# Revit family: Hager-UNIVERS-Surface_mounted-IP44-With_Cover-With_DIN-NoHosted-IE-en
name_source: partatom
category: Electrical Equipment
units: mm (PartAtom-declared; Revit-internal decimal feet)

## family parameters
Always vertical = Yes
Cut with Voids When Loaded = No
Maintain Annotation Orientation = No
Panel Configuration = Two Columns, Circuits Across
Part Type = Panelboard
Room Calculation Point = No
Round Connector Dimension = Use Diameter
Shared = No
Work Plane-Based = Yes

## types (20) — shared parameters
Code hager = ADD-EC000214_EU
Default Elevation = 1200 mm
EF000003 - Mounting method = Surface mounted
EF000007 - Colour = White
EF000024 - UV resistant = No
EF000049 - Depth = 165 mm
EF000116 - RAL-number = 9010
EF000118 - With mounting plate = No
EF000218 - Built-in depth = 161 mm  [stored 0.528215 ft]
EF001062 - EMC-version = No
EF001088 - Extension possible = Yes
EF001134 - DIN-rail = Yes
EF004462 - Type of closure = Other
EF005474 - Degree of protection (IP) = IP44
EF006244 - Transparent cover/door = No
EF006306 - With lock = No
EF009212 - Cover model = With notch
EF015776 - Earthing terminal block = No
EF015777 - Neutral terminal block = Yes
EF015941 - Signal passing door = No
ETIM class code = EC000214
ETIM class name = Small distribution board
HG000002-With door or cover = Yes
HG000003-Range = UNIVERS
HG000005-Thickness = 2 mm  [stored 0.00656168 ft]
HG000006-Flush mounted = No
HG000011-Empty rows from bottom = No
HG000012-Door swing angle = 90.00°
HG000013-Door on the left = No
HG000014-Door on the right = Yes
HG000015-Clearance visibility = Yes
HG000016-Door 3D visibility = Yes
HG000017-Distance between poles = 18 mm  [stored 0.0590551 ft]
HG000060-RAL-number = 9010
HG000099-Onfly Template ID = 507532
Manufacturer = Hager
Name BIM&CO = Electricity
Name hager = ADD_Enclosures_EC000214
Reference = Template-Enclosure_EU-EC000214
Uniformat = Low Tension Service & Dist.
Uniformat code = D501001
zero-valued in all types: EF001131 - Inner depth, HG000007-Number of empty columns, HG000008-Number of empty rows

## per-type parameters (varying)
| type | BC_METADATA | EF000008 - Width | EF000040 - Height | EF000266 - Number of rows | EF000332 - Built-in height | EF000846 - Built-in width | EF002950 - Width in number of modular spacings | HG000001-Number of columns | HG000004-Manufacturer reference | HG000009-Double swing door | HG000010-Asymmetric doors | HGEF000266-Number of rows | HGEF002950-Width in number of modular spacings |
| UNIVERS-Surface_mounted_W300_H500_D165_12_Modular_Spacing-FWB31 | {"ObjectGuid":"87d1702a-8fc3-4392-9d8b-29cae2940906","ModelGuid":"894203d7-2d7f-404a-984e-4a048ff082d1","VariantGuid":"fb002c13-881c-4551-97f2-6654b2d32c52","Revision":"#3","VariantName":"UNIVERS-Surface_mounted_W300_H500_D165_12_Modular_Spacing-FWB31"} | 300 mm | 500 mm  [stored 1.64042 ft] | 3 | 500 mm  [stored 1.64042 ft] | 300 mm | 12 | 1 | FWB31 | No | No | 3 | 12 |
| UNIVERS-Surface_mounted_W550_H500_D165_24_Modular_Spacing-FWB32 | {"ObjectGuid":"87d1702a-8fc3-4392-9d8b-29cae2940906","ModelGuid":"894203d7-2d7f-404a-984e-4a048ff082d1","VariantGuid":"cee11cdb-fcee-4029-a44f-e8bf54190ad9","Revision":"#3","VariantName":"UNIVERS-Surface_mounted_W550_H500_D165_24_Modular_Spacing-FWB32"} | 550 mm | 500 mm  [stored 1.64042 ft] | 3 | 500 mm  [stored 1.64042 ft] | 550 mm | 24 | 2 | FWB32 | No | No | 3 | 24 |
| UNIVERS-Surface_mounted_W800_H500_D165_36_Modular_Spacing-FWB33 | {"ObjectGuid":"87d1702a-8fc3-4392-9d8b-29cae2940906","ModelGuid":"894203d7-2d7f-404a-984e-4a048ff082d1","VariantGuid":"9ffd5afd-2b9f-452c-9877-37d7ab24ad53","Revision":"#3","VariantName":"UNIVERS-Surface_mounted_W800_H500_D165_36_Modular_Spacing-FWB33"} | 800 mm  [stored 2.62467 ft] | 500 mm  [stored 1.64042 ft] | 3 | 500 mm  [stored 1.64042 ft] | 800 mm  [stored 2.62467 ft] | 36 | 3 | FWB33 | Yes | Yes | 3 | 36 |
| UNIVERS-Surface_mounted_W1050_H500_D165_48_Modular_Spacing-FWB34 | {"ObjectGuid":"87d1702a-8fc3-4392-9d8b-29cae2940906","ModelGuid":"894203d7-2d7f-404a-984e-4a048ff082d1","VariantGuid":"757fb0db-eacd-4dbe-9c26-48be6830e068","Revision":"#3","VariantName":"UNIVERS-Surface_mounted_W1050_H500_D165_48_Modular_Spacing-FWB34"} | 1050 mm  [stored 3.44488 ft] | 500 mm  [stored 1.64042 ft] | 3 | 500 mm  [stored 1.64042 ft] | 1050 mm  [stored 3.44488 ft] | 48 | 4 | FWB34 | Yes | No | 3 | 48 |
| UNIVERS-Surface_mounted_W300_H650_D165_12_Modular_Spacing-FWB41 | {"ObjectGuid":"87d1702a-8fc3-4392-9d8b-29cae2940906","ModelGuid":"894203d7-2d7f-404a-984e-4a048ff082d1","VariantGuid":"200c4517-b822-4654-bec3-323ac2ee224b","Revision":"#3","VariantName":"UNIVERS-Surface_mounted_W300_H650_D165_12_Modular_Spacing-FWB41"} | 300 mm | 650 mm  [stored 2.13255 ft] | 4 | 650 mm  [stored 2.13255 ft] | 300 mm | 12 | 1 | FWB41 | No | No | 4 | 12 |
| UNIVERS-Surface_mounted_W550_H650_D165_24_Modular_Spacing-FWB42 | {"ObjectGuid":"87d1702a-8fc3-4392-9d8b-29cae2940906","ModelGuid":"894203d7-2d7f-404a-984e-4a048ff082d1","VariantGuid":"df44d009-7728-4836-95ee-009f0ac16905","Revision":"#3","VariantName":"UNIVERS-Surface_mounted_W550_H650_D165_24_Modular_Spacing-FWB42"} | 550 mm | 650 mm  [stored 2.13255 ft] | 4 | 650 mm  [stored 2.13255 ft] | 550 mm | 24 | 2 | FWB42 | No | No | 4 | 24 |
| UNIVERS-Surface_mounted_W800_H650_D165_36_Modular_Spacing-FWB43 | {"ObjectGuid":"87d1702a-8fc3-4392-9d8b-29cae2940906","ModelGuid":"894203d7-2d7f-404a-984e-4a048ff082d1","VariantGuid":"1a2c2fab-c1f9-4678-af95-63d509a17314","Revision":"#3","VariantName":"UNIVERS-Surface_mounted_W800_H650_D165_36_Modular_Spacing-FWB43"} | 800 mm  [stored 2.62467 ft] | 650 mm  [stored 2.13255 ft] | 4 | 650 mm  [stored 2.13255 ft] | 800 mm  [stored 2.62467 ft] | 36 | 3 | FWB43 | Yes | Yes | 4 | 36 |
| UNIVERS-Surface_mounted_W1050_H650_D165_48_Modular_Spacing-FWB44 | {"ObjectGuid":"87d1702a-8fc3-4392-9d8b-29cae2940906","ModelGuid":"894203d7-2d7f-404a-984e-4a048ff082d1","VariantGuid":"95f7c8aa-e01f-4d5c-9763-2ded6d1ccbba","Revision":"#3","VariantName":"UNIVERS-Surface_mounted_W1050_H650_D165_48_Modular_Spacing-FWB44"} | 1050 mm  [stored 3.44488 ft] | 650 mm  [stored 2.13255 ft] | 4 | 650 mm  [stored 2.13255 ft] | 1050 mm  [stored 3.44488 ft] | 48 | 4 | FWB44 | Yes | No | 4 | 48 |
| UNIVERS-Surface_mounted_W300_H800_D165_12_Modular_Spacing-FWB51 | {"ObjectGuid":"87d1702a-8fc3-4392-9d8b-29cae2940906","ModelGuid":"894203d7-2d7f-404a-984e-4a048ff082d1","VariantGuid":"bc364827-2a88-4f4d-b013-22060a447f94","Revision":"#3","VariantName":"UNIVERS-Surface_mounted_W300_H800_D165_12_Modular_Spacing-FWB51"} | 300 mm | 800 mm  [stored 2.62467 ft] | 5 | 800 mm  [stored 2.62467 ft] | 300 mm | 12 | 1 | FWB51 | No | No | 5 | 12 |
| UNIVERS-Surface_mounted_W550_H800_D165_24_Modular_Spacing-FWB52 | {"ObjectGuid":"87d1702a-8fc3-4392-9d8b-29cae2940906","ModelGuid":"894203d7-2d7f-404a-984e-4a048ff082d1","VariantGuid":"4fe331b8-bf32-456e-aabb-ef4181844985","Revision":"#3","VariantName":"UNIVERS-Surface_mounted_W550_H800_D165_24_Modular_Spacing-FWB52"} | 550 mm | 800 mm  [stored 2.62467 ft] | 5 | 800 mm  [stored 2.62467 ft] | 550 mm | 24 | 2 | FWB52 | No | No | 5 | 24 |
| UNIVERS-Surface_mounted_W800_H800_D165_36_Modular_Spacing-FWB53 | {"ObjectGuid":"87d1702a-8fc3-4392-9d8b-29cae2940906","ModelGuid":"894203d7-2d7f-404a-984e-4a048ff082d1","VariantGuid":"a2cdd5c0-b026-411c-bbdb-f125d01b5ec7","Revision":"#3","VariantName":"UNIVERS-Surface_mounted_W800_H800_D165_36_Modular_Spacing-FWB53"} | 800 mm  [stored 2.62467 ft] | 800 mm  [stored 2.62467 ft] | 5 | 800 mm  [stored 2.62467 ft] | 800 mm  [stored 2.62467 ft] | 36 | 3 | FWB53 | Yes | Yes | 5 | 36 |
| UNIVERS-Surface_mounted_W1050_H800_D165_48_Modular_Spacing-FWB54 | {"ObjectGuid":"87d1702a-8fc3-4392-9d8b-29cae2940906","ModelGuid":"894203d7-2d7f-404a-984e-4a048ff082d1","VariantGuid":"f753a9e4-5433-4262-89b7-cb5eb92284fa","Revision":"#3","VariantName":"UNIVERS-Surface_mounted_W1050_H800_D165_48_Modular_Spacing-FWB54"} | 1050 mm  [stored 3.44488 ft] | 800 mm  [stored 2.62467 ft] | 5 | 800 mm  [stored 2.62467 ft] | 1050 mm  [stored 3.44488 ft] | 48 | 4 | FWB54 | Yes | No | 5 | 48 |
| UNIVERS-Surface_mounted_W300_H950_D165_12_Modular_Spacing-FWB61 | {"ObjectGuid":"87d1702a-8fc3-4392-9d8b-29cae2940906","ModelGuid":"894203d7-2d7f-404a-984e-4a048ff082d1","VariantGuid":"ea57bed8-9cc6-421a-9c08-9408b4ac2fac","Revision":"#3","VariantName":"UNIVERS-Surface_mounted_W300_H950_D165_12_Modular_Spacing-FWB61"} | 300 mm | 950 mm  [stored 3.1168 ft] | 6 | 950 mm  [stored 3.1168 ft] | 300 mm | 12 | 1 | FWB61 | No | No | 6 | 12 |
| UNIVERS-Surface_mounted_W550_H950_D165_24_Modular_Spacing-FWB62 | {"ObjectGuid":"87d1702a-8fc3-4392-9d8b-29cae2940906","ModelGuid":"894203d7-2d7f-404a-984e-4a048ff082d1","VariantGuid":"2ade9510-fd3f-42d4-b714-e9838d2b98de","Revision":"#3","VariantName":"UNIVERS-Surface_mounted_W550_H950_D165_24_Modular_Spacing-FWB62"} | 550 mm | 950 mm  [stored 3.1168 ft] | 6 | 950 mm  [stored 3.1168 ft] | 550 mm | 24 | 2 | FWB62 | No | No | 6 | 24 |
| UNIVERS-Surface_mounted_W800_H950_D165_36_Modular_Spacing-FWB63 | {"ObjectGuid":"87d1702a-8fc3-4392-9d8b-29cae2940906","ModelGuid":"894203d7-2d7f-404a-984e-4a048ff082d1","VariantGuid":"2e33cdc1-9ceb-454d-ada8-b06cd376f0f2","Revision":"#3","VariantName":"UNIVERS-Surface_mounted_W800_H950_D165_36_Modular_Spacing-FWB63"} | 800 mm  [stored 2.62467 ft] | 950 mm  [stored 3.1168 ft] | 6 | 950 mm  [stored 3.1168 ft] | 800 mm  [stored 2.62467 ft] | 36 | 3 | FWB63 | Yes | Yes | 6 | 36 |
| UNIVERS-Surface_mounted_W1050_H950_D165_48_Modular_Spacing-FWB64 | {"ObjectGuid":"87d1702a-8fc3-4392-9d8b-29cae2940906","ModelGuid":"894203d7-2d7f-404a-984e-4a048ff082d1","VariantGuid":"eea25d1c-1cde-46e6-98c6-91d3e82bafb2","Revision":"#3","VariantName":"UNIVERS-Surface_mounted_W1050_H950_D165_48_Modular_Spacing-FWB64"} | 1050 mm  [stored 3.44488 ft] | 950 mm  [stored 3.1168 ft] | 6 | 950 mm  [stored 3.1168 ft] | 1050 mm  [stored 3.44488 ft] | 48 | 4 | FWB64 | Yes | No | 6 | 48 |
| UNIVERS-Surface_mounted_W300_H1100_D165_12_Modular_Spacing-FWB71 | {"ObjectGuid":"87d1702a-8fc3-4392-9d8b-29cae2940906","ModelGuid":"894203d7-2d7f-404a-984e-4a048ff082d1","VariantGuid":"6917e487-7303-4e08-b469-b48b9a206a82","Revision":"#3","VariantName":"UNIVERS-Surface_mounted_W300_H1100_D165_12_Modular_Spacing-FWB71"} | 300 mm | 1100 mm | 7 | 1100 mm | 300 mm | 12 | 1 | FWB71 | No | No | 7 | 12 |
| UNIVERS-Surface_mounted_W550_H1100_D165_24_Modular_Spacing-FWB72 | {"ObjectGuid":"87d1702a-8fc3-4392-9d8b-29cae2940906","ModelGuid":"894203d7-2d7f-404a-984e-4a048ff082d1","VariantGuid":"88ab4844-a65e-43c1-a725-39705998ae2f","Revision":"#3","VariantName":"UNIVERS-Surface_mounted_W550_H1100_D165_24_Modular_Spacing-FWB72"} | 550 mm | 1100 mm | 7 | 1100 mm | 550 mm | 24 | 2 | FWB72 | No | No | 7 | 24 |
| UNIVERS-Surface_mounted_W800_H1100_D165_36_Modular_Spacing-FWB73 | {"ObjectGuid":"87d1702a-8fc3-4392-9d8b-29cae2940906","ModelGuid":"894203d7-2d7f-404a-984e-4a048ff082d1","VariantGuid":"dab814c9-129b-42c3-89cb-a7b9031da608","Revision":"#3","VariantName":"UNIVERS-Surface_mounted_W800_H1100_D165_36_Modular_Spacing-FWB73"} | 800 mm  [stored 2.62467 ft] | 1100 mm | 7 | 1100 mm | 800 mm  [stored 2.62467 ft] | 36 | 3 | FWB73 | Yes | Yes | 7 | 36 |
| UNIVERS-Surface_mounted_W1050_H1100_D165_48_Modular_Spacing-FWB74 | {"ObjectGuid":"87d1702a-8fc3-4392-9d8b-29cae2940906","ModelGuid":"894203d7-2d7f-404a-984e-4a048ff082d1","VariantGuid":"a07db3fd-8317-4785-8ba8-61be3afb26dc","Revision":"#3","VariantName":"UNIVERS-Surface_mounted_W1050_H1100_D165_48_Modular_Spacing-FWB74"} | 1050 mm  [stored 3.44488 ft] | 1100 mm | 7 | 1100 mm | 1050 mm  [stored 3.44488 ft] | 48 | 4 | FWB74 | Yes | No | 7 | 48 |

note: [stored X ft] marks values corroborated as IEEE doubles in the binary element streams (Revit-internal decimal feet)

## geometry (parser evidence)
native form markers: Sweep x15
no freeform markers — native parametric forms only
